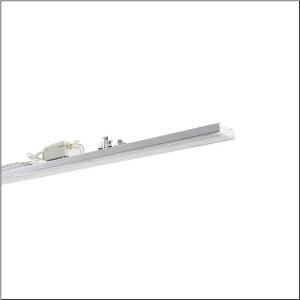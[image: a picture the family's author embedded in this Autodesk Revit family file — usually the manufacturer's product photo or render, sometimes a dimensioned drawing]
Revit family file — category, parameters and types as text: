
# Revit family: licross_21_recessed_ho_52tl12de475m
name_source: partatom
category: Lighting Fixtures
units: mm (PartAtom-declared; Revit-internal decimal feet)

## family parameters
Cut with Voids When Loaded = No
Host = Face
Light Source = No
Part Type = Normal
Room Calculation Point = No
Round Connector Dimension = Use Diameter
Shared = No

## types (1)
- --- (1 x LED, 7500 lm, 44.1 W, 4000K)
    Apparent Load = 44 VA
    CIE Flux Codes = 69 91 98 100 100
    Color Rendering = 80
    Color Temperature = 4000K
    Default Elevation = 1800 mm
    Description = Licross 21 Recessed HO, luminaire insert, of sheet steel, galvanised, coil coated, white, length: 750mm, width: 66mm, height: 67mm, LED rated luminous flux: 7.500lm, light colour: 840, SDCM (Standard Deviation of Colour Matching)MacAdam ≤ 3 SDCM (initial), control gear: DALI 2, with plug, 5-pole, with phase selection, mains connection: 220..240V, AC, 50/60Hz, rated input power: 44W, internal wiring halogen-free, primary light control with lens, of plastic, primary optical cover: cover, of PMMA, light emission: direct distribution, primary light characteristic: symmetric, protection rating (complete): IP40, insulation class (complete): insulation class I (protective earthing), certification: CE, ENEC, VDE, UKCA, protection symbol: D if used in an environment without relevant dust loads with corresponding accessories, impact resistance: IK06, permissible ambient temperature for indoor applications: -25..+30°C, corresponds to IFS (International Featured Standards) requirements for safety and quality in the food industry, reducing of maximum allowable ambient temperature of 5°C with ceiling mounting, LABS conformity tested according to VDMA 24364:2018-05, The light source and the operating device comply with the requirements of the Ecodesign Regulation (EU) 2019/2020 and are replaceable in accordance with this regulation, packaging unit: 1 piece
    Height = 58 mm
    Lamp = 1 x LED
    Lamp Light Flux = 7500 lm
    Lamp Power = 44.1 W
    Lamp count = 1
    Length = 750 mm
    Luminous efficacy = 170 lm/W
    Manufacturer = Siteco
    ModVariant = No
    Model = 52TL12DE475M
    Mounting Place = Ceiling
    Mounting Type = Pendant
    Number of Poles = 1
    OnlyDefault = Yes
    Power Factor = 1
    Product Name = Licross 21 Recessed HO
    Product group = luminaire insert | ceiling pendant
    ProductGroupID = 901
    Protection Class = Protection class I
    Protection Degree = IP 40
    RLX_Detail_Level = 1
    RLX_Emergency_Light_Flux = 0 lm
    RLX_Emergency_Type = 0
    RLX_Emergency_Type_DB = No
    RlxData = <blob elided: 29821 chars, md5=c937cf95>
    Socket = socket
    Standby Power = 0 W
    System Light Flux = 7500 lm
    System Power = 44 W
    Type Comments = factory setting: luminous flux: 100 % | dim-lin: 254 | 484 mA
    Type Image = l_1296930.jpg
    URL = http://relux.com
    VarID = @adj_118491
    Voltage = 0 V
    Weight = 0.00 kg
    Width = 66 mm

## geometry (parser evidence)
native form markers: Blend x4, Sweep x8
no freeform markers — native parametric forms only
